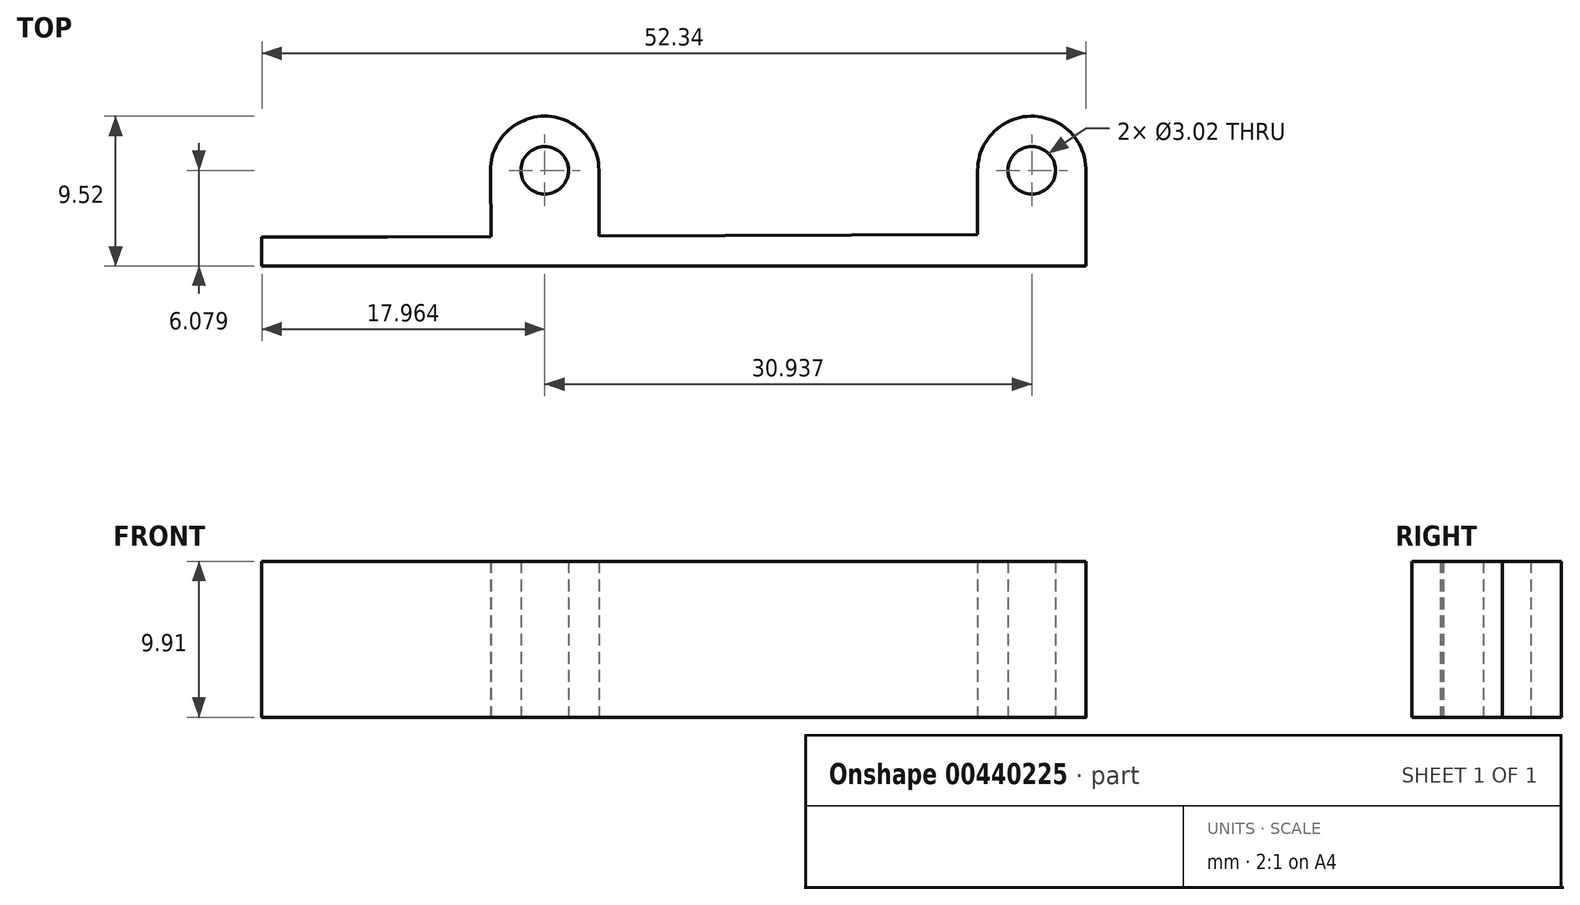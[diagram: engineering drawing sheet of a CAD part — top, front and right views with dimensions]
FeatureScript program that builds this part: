
annotation { "Feature Type Name" : "Feature", "Feature Type Description" : "" }
export const myFeature = defineFeature(function(context is Context, id is Id, definition is map)
    precondition{}
    {
        {
            var Q0;
            Q0=qCreatedBy(makeId("Top.planeOp"),FACE);
            var sketch = newSketch(context, id + "F0", { "sketchPlane" : qUnion([Q0])});
            skLineSegment(sketch, "E0.top", {"start": v(-12.93, 8.15) * mm, "end": v(24.85, 8.15) * mm});
            skCircle(sketch, "E1", {"center": v(-9.52, 14.23) * mm, "radius": 1.51 * mm});
            skCircle(sketch, "E2", {"center": v(21.42, 14.23) * mm, "radius": 1.51 * mm});
            skCircle(sketch, "E3", {"center": v(-9.52, 14.23) * mm, "radius": 3.44 * mm});
            skCircle(sketch, "E4", {"center": v(21.42, 14.23) * mm, "radius": 3.44 * mm});
            skLineSegment(sketch, "E5", {"start": v(-6.07, 14.23) * mm, "end": v(-6.07, 10.05) * mm});
            skLineSegment(sketch, "E6", {"start": v(-12.96, 14.23) * mm, "end": v(-12.93, 8.15) * mm});
            skLineSegment(sketch, "E7", {"start": v(17.98, 14.23) * mm, "end": v(17.98, 10.16) * mm});
            skLineSegment(sketch, "E8", {"start": v(24.85, 10.19) * mm, "end": v(-14.72, 10.01) * mm});
            skLineSegment(sketch, "E9", {"start": v(-14.72, 10.01) * mm, "end": v(-19.53, 10) * mm});
            skLineSegment(sketch, "E10", {"start": v(-19.53, 10) * mm, "end": v(-19.53, 8.15) * mm});
            skLineSegment(sketch, "E11", {"start": v(-19.53, 8.15) * mm, "end": v(-12.93, 8.15) * mm});
            skLineSegment(sketch, "E12", {"start": v(24.85, 13.9) * mm, "end": v(24.85, 8.15) * mm});
            skLineSegment(sketch, "E13", {"start": v(-19.53, 10) * mm, "end": v(-27.48, 10) * mm});
            skLineSegment(sketch, "E14", {"start": v(-27.48, 10) * mm, "end": v(-27.48, 8.15) * mm});
            skLineSegment(sketch, "E15", {"start": v(-27.48, 8.15) * mm, "end": v(-19.53, 8.15) * mm});
            skSolve(sketch);
        }
        {
            var Q0;
            Q0 = qSketchRegion(id + "F0", true);
            extrude(context, id + "F1", {"entities" : qUnion([Q0]), "depth" : 9.9 * mm});
        }
    });
